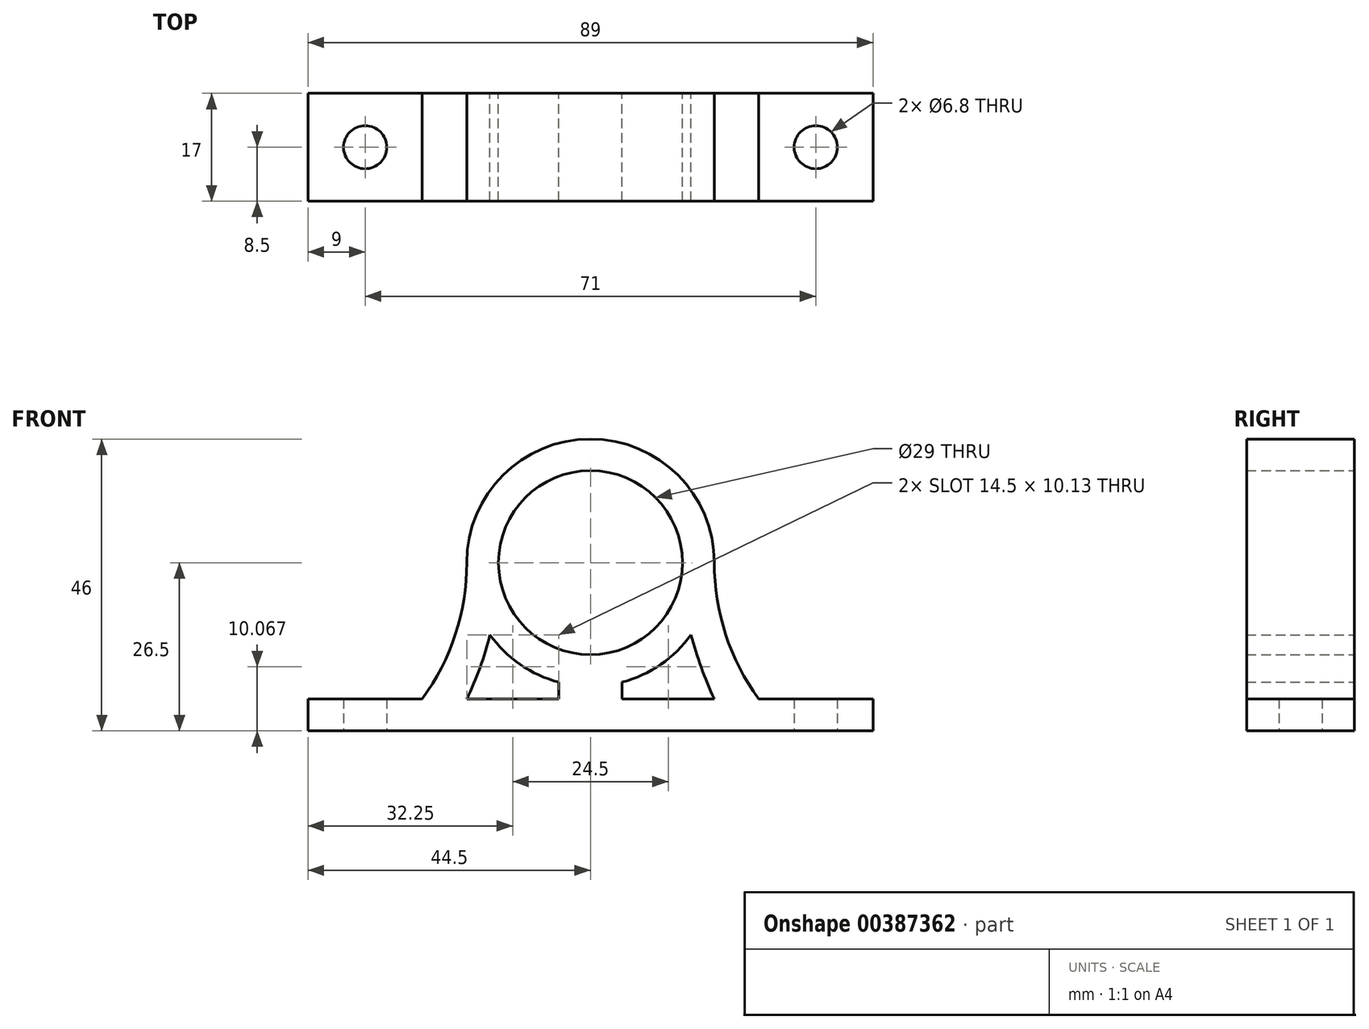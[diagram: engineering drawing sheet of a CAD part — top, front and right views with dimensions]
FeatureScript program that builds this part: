
annotation { "Feature Type Name" : "Feature", "Feature Type Description" : "" }
export const myFeature = defineFeature(function(context is Context, id is Id, definition is map)
    precondition{}
    {
        {
            var Q0;
            Q0=qCreatedBy(makeId("Front.planeOp"),FACE);
            var sketch = newSketch(context, id + "F0", { "sketchPlane" : qUnion([Q0])});
            skCircle(sketch, "E0", {"center": v(0, 0) * mm, "radius": 14.5 * mm});
            skPoint(sketch, "E1", {"position": v(0, -26.5) * mm});
            skPoint(sketch, "E2", {"position": v(-26.5, -26.5) * mm});
            skPoint(sketch, "E3", {"position": v(26.5, -26.5) * mm});
            skLineSegment(sketch, "E4", {"start": v(-26.5, -26.5) * mm, "end": v(-35.5, -26.5) * mm, "construction": true});
            skLineSegment(sketch, "E5", {"start": v(26.5, -26.5) * mm, "end": v(35.5, -26.5) * mm, "construction": true});
            skPoint(sketch, "E6", {"position": v(-35.5, -26.5) * mm});
            skPoint(sketch, "E7", {"position": v(35.5, -26.5) * mm});
            skLineSegment(sketch, "E8", {"start": v(-26.5, -26.5) * mm, "end": v(-44.5, -26.5) * mm, "construction": true});
            skLineSegment(sketch, "E9", {"start": v(26.5, -26.5) * mm, "end": v(44.5, -26.5) * mm, "construction": true});
            skPoint(sketch, "E10", {"position": v(-44.5, -26.5) * mm});
            skPoint(sketch, "E11", {"position": v(44.5, -26.5) * mm});
            skLineSegment(sketch, "E12", {"start": v(-44.5, -26.5) * mm, "end": v(-44.5, -21.5) * mm});
            skLineSegment(sketch, "E13", {"start": v(-44.5, -26.5) * mm, "end": v(44.5, -26.5) * mm});
            skLineSegment(sketch, "E14", {"start": v(44.5, -26.5) * mm, "end": v(44.5, -21.5) * mm});
            skPoint(sketch, "E15", {"position": v(-19.5, 0) * mm});
            skPoint(sketch, "E16", {"position": v(19.5, 0) * mm});
            skArc(sketch, "E17", {"start": v(-19.5, 0) * mm, "mid": v(0, 19.5) * mm, "end": v(19.5, 0) * mm});
            skLineSegment(sketch, "E18", {"start": v(-26.5, -26.5) * mm, "end": v(-26.5, -21.5) * mm, "construction": true});
            skLineSegment(sketch, "E19", {"start": v(26.5, -26.5) * mm, "end": v(26.5, -21.5) * mm, "construction": true});
            skLineSegment(sketch, "E20", {"start": v(-19.5, -21.5) * mm, "end": v(19.5, -21.5) * mm, "construction": true});
            skCircle(sketch, "E21", {"center": v(0, 0) * mm, "radius": 24.5 * mm, "construction": true});
            skPoint(sketch, "E22", {"position": v(-11.75, -21.5) * mm});
            skPoint(sketch, "E23", {"position": v(11.75, -21.5) * mm});
            skArc(sketch, "E24", {"start": v(-26.5, -21.5) * mm, "mid": v(-21.3, -11.3) * mm, "end": v(-19.5, 0) * mm});
            skArc(sketch, "E25", {"start": v(19.5, 0) * mm, "mid": v(21.3, -11.3) * mm, "end": v(26.5, -21.5) * mm});
            skPoint(sketch, "E26", {"position": v(-14.5, 0) * mm});
            skPoint(sketch, "E27", {"position": v(14.5, 0) * mm});
            skLineSegment(sketch, "E28", {"start": v(-14.5, 0) * mm, "end": v(-14.5, -21.5) * mm, "construction": true});
            skLineSegment(sketch, "E29", {"start": v(14.5, 0) * mm, "end": v(14.5, -21.5) * mm, "construction": true});
            skLineSegment(sketch, "E30", {"start": v(0, -21.5) * mm, "end": v(-5, -21.5) * mm, "construction": true});
            skLineSegment(sketch, "E31", {"start": v(0, -21.5) * mm, "end": v(5, -21.5) * mm, "construction": true});
            skPoint(sketch, "E32", {"position": v(-15.84, -11.37) * mm});
            skPoint(sketch, "E33", {"position": v(15.84, -11.37) * mm});
            skArc(sketch, "E34", {"start": v(-15.84, -11.37) * mm, "mid": v(0, -19.5) * mm, "end": v(15.84, -11.37) * mm});
            skLineSegment(sketch, "E35", {"start": v(-44.5, -21.5) * mm, "end": v(-26.5, -21.5) * mm});
            skLineSegment(sketch, "E36", {"start": v(-19.5, -21.5) * mm, "end": v(19.5, -21.5) * mm});
            skLineSegment(sketch, "E37", {"start": v(26.5, -21.5) * mm, "end": v(44.5, -21.5) * mm});
            skLineSegment(sketch, "E38", {"start": v(-5, -21.5) * mm, "end": v(-5, -18.85) * mm});
            skLineSegment(sketch, "E39", {"start": v(5, -21.5) * mm, "end": v(5, -18.85) * mm});
            skArc(sketch, "E40", {"start": v(-19.5, -21.5) * mm, "mid": v(-17.4, -16.53) * mm, "end": v(-15.84, -11.37) * mm});
            skArc(sketch, "E41", {"start": v(15.84, -11.37) * mm, "mid": v(17.45, -16.51) * mm, "end": v(19.5, -21.5) * mm});
            skSolve(sketch);
        }
        {
            var Q0;
            Q0=makeQuery(id+"F0.imprint","IMPRINT",FACE,{"disambiguationData":[TD([[makeQuery(id+"F0.imprint","IMPRINT",EDGE,{"derivedFrom":sQuery(id+"F0.wireOp",EDGE,"E0")}),-1.0]])]});
            var Q1;
            {var subQ0=sQuery(id+"F0.wireOp",EDGE,"E38");Q1=makeQuery(id+"F0.imprint","IMPRINT",FACE,{"disambiguationData":[TD([[makeQuery(id+"F0.imprint","IMPRINT",EDGE,{"derivedFrom":subQ0}),-1.0]])]});}
            extrude(context, id + "F1", {"entities" : qUnion([Q0, Q1]), "depth" : 17 * mm, "offsetDistance" : 25 * mm});
        }
        {
            var Q0;
            Q0=makeQuery(id+"F1.opExtrude","SWEPT_FACE",FACE,{"disambiguationData":[OSD([sQuery(id+"F0.wireOp",EDGE,"E13")])]});
            var sketch = newSketch(context, id + "F2", { "sketchPlane" : qUnion([Q0])});
            skPoint(sketch, "E42", {"position": v(-44.5, 17) * mm});
            skLineSegment(sketch, "E43", {"start": v(-44.5, 17) * mm, "end": v(-44.5, 8.5) * mm, "construction": true});
            skLineSegment(sketch, "E44", {"start": v(-44.5, 8.5) * mm, "end": v(44.5, 8.5) * mm, "construction": true});
            skLineSegment(sketch, "E45", {"start": v(-44.5, 8.5) * mm, "end": v(-35.5, 8.5) * mm, "construction": true});
            skLineSegment(sketch, "E46", {"start": v(44.5, 8.5) * mm, "end": v(35.5, 8.5) * mm, "construction": true});
            skPoint(sketch, "E47", {"position": v(-35.5, 8.5) * mm});
            skPoint(sketch, "E48", {"position": v(35.5, 8.5) * mm});
            skCircle(sketch, "E49", {"center": v(-35.5, 8.5) * mm, "radius": 3.4 * mm});
            skCircle(sketch, "E50", {"center": v(35.5, 8.5) * mm, "radius": 3.4 * mm});
            skSolve(sketch);
        }
        {
            var Q0;
            Q0=makeQuery(id+"F2.imprint","IMPRINT",FACE,{"disambiguationData":[TD([[makeQuery(id+"F2.imprint","IMPRINT",EDGE,{"derivedFrom":sQuery(id+"F2.wireOp",EDGE,"E49")}),1.0]])]});
            var Q1;
            Q1=makeQuery(id+"F2.imprint","IMPRINT",FACE,{"disambiguationData":[TD([[makeQuery(id+"F2.imprint","IMPRINT",EDGE,{"derivedFrom":sQuery(id+"F2.wireOp",EDGE,"E50")}),1.0]])]});
            extrude(context, id + "F3", {"entities" : qUnion([Q0, Q1]), "operationType" : NewBodyOperationType.REMOVE, "endBound" : BoundingType.THROUGH_ALL, "oppositeDirection" : true, "depth" : 25 * mm, "offsetDistance" : 25 * mm});
        }
    });
